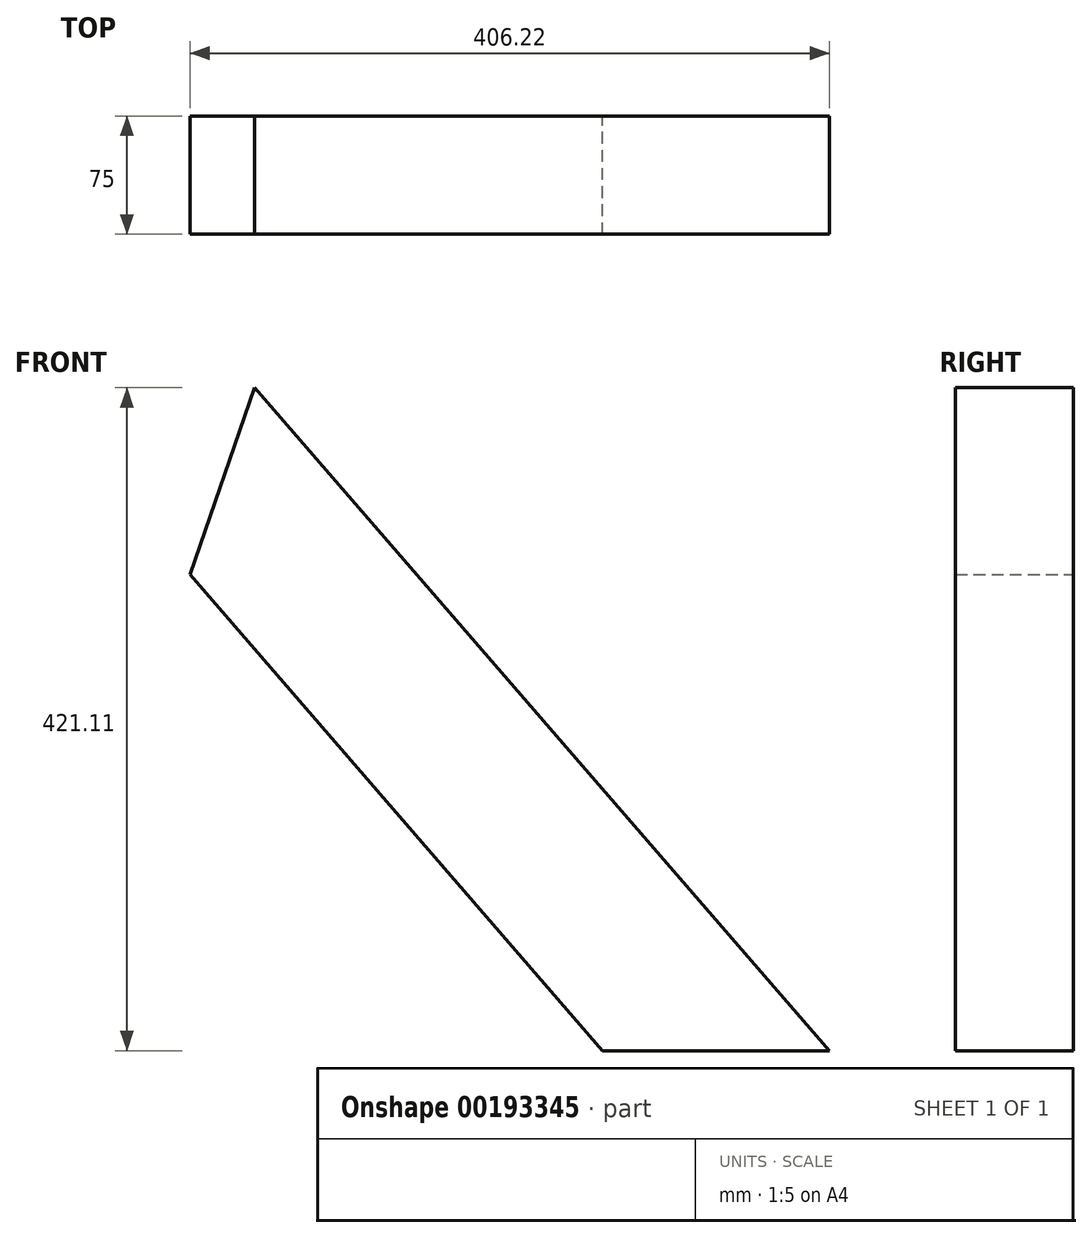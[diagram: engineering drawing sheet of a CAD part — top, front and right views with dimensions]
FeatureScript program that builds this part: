
annotation { "Feature Type Name" : "Feature", "Feature Type Description" : "" }
export const myFeature = defineFeature(function(context is Context, id is Id, definition is map)
    precondition{}
    {
        {
            var Q0;
            Q0=qCreatedBy(makeId("Front.planeOp"),FACE);
            var sketch = newSketch(context, id + "F0", { "sketchPlane" : qUnion([Q0])});
            skLineSegment(sketch, "E0", {"start": v(-162.5, -32.08) * mm, "end": v(99.61, -334.37) * mm});
            skLineSegment(sketch, "E1", {"start": v(-162.5, -32.08) * mm, "end": v(-203.58, -150.9) * mm});
            skLineSegment(sketch, "E2", {"start": v(-203.58, -150.9) * mm, "end": v(58.54, -453.19) * mm});
            skPoint(sketch, "E3.start.orphan", {"position": v(-23.26, -358.85) * mm});
            skLineSegment(sketch, "E4", {"start": v(58.54, -453.19) * mm, "end": v(99.61, -334.37) * mm});
            skLineSegment(sketch, "E5", {"start": v(58.54, -453.19) * mm, "end": v(202.64, -453.19) * mm});
            skLineSegment(sketch, "E6", {"start": v(99.61, -334.37) * mm, "end": v(202.64, -453.19) * mm});
            skSolve(sketch);
        }
        {
            var Q0;
            Q0=qSketchRegion(id+"F0",true);
            extrude(context, id + "F1", {"entities" : qUnion([Q0]), "endBound" : BoundingType.SYMMETRIC, "depth" : 75 * mm});
        }
    });
